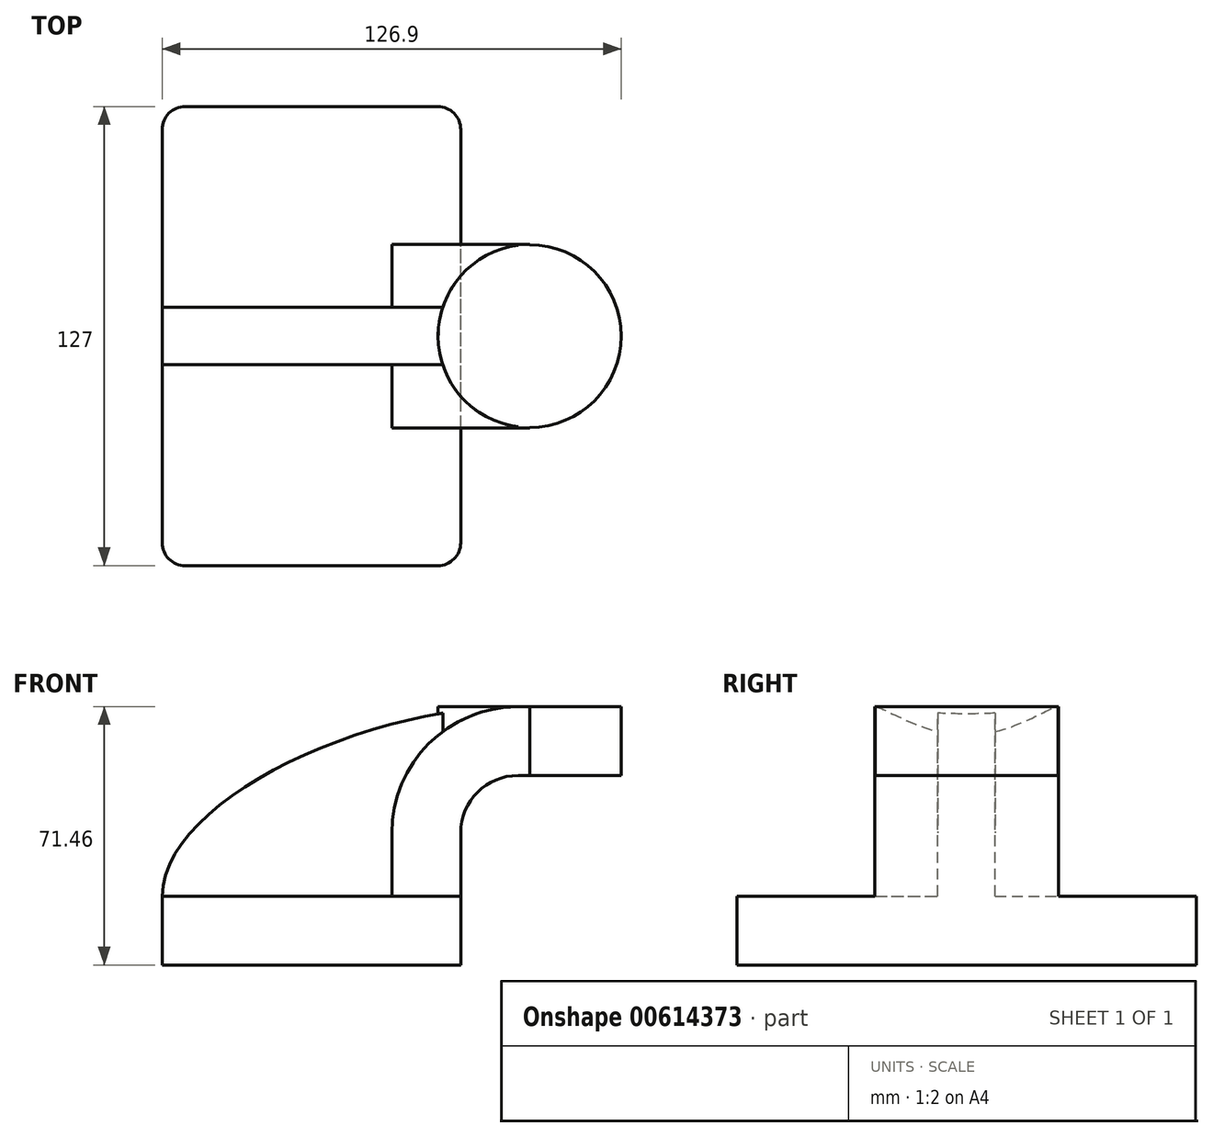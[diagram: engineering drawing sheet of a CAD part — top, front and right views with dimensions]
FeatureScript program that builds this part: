
annotation { "Feature Type Name" : "Feature", "Feature Type Description" : "" }
export const myFeature = defineFeature(function(context is Context, id is Id, definition is map)
    precondition{}
    {
        {
            var Q0;
            Q0=qCreatedBy(makeId("Front.planeOp"),FACE);
            var sketch = newSketch(context, id + "F0", { "sketchPlane" : qUnion([Q0])});
            skLineSegment(sketch, "E0.bottom", {"start": v(41.28, -9.52) * mm, "end": v(-41.28, -9.53) * mm});
            skLineSegment(sketch, "E0.top", {"start": v(41.28, 9.53) * mm, "end": v(-41.28, 9.53) * mm});
            skLineSegment(sketch, "E0.left", {"start": v(41.28, -9.52) * mm, "end": v(41.28, 9.53) * mm});
            skLineSegment(sketch, "E0.right", {"start": v(-41.28, -9.53) * mm, "end": v(-41.28, 9.53) * mm});
            skPoint(sketch, "E0.middle", {"position": v(0, 0) * mm});
            skLineSegment(sketch, "E1.bottom", {"start": v(111.12, 38.1) * mm, "end": v(60.33, 38.1) * mm});
            skLineSegment(sketch, "E1.top", {"start": v(111.12, 66.68) * mm, "end": v(60.33, 66.68) * mm});
            skLineSegment(sketch, "E1.left", {"start": v(111.12, 38.1) * mm, "end": v(111.12, 66.68) * mm});
            skLineSegment(sketch, "E1.right", {"start": v(60.33, 38.1) * mm, "end": v(60.33, 66.68) * mm});
            skPoint(sketch, "E1.middle", {"position": v(85.72, 52.39) * mm});
            skLineSegment(sketch, "E2", {"start": v(41.28, 9.53) * mm, "end": v(41.28, 27) * mm});
            skArc(sketch, "E3", {"start": v(41.27, 27) * mm, "mid": v(45.92, 38.23) * mm, "end": v(57.15, 42.88) * mm});
            skLineSegment(sketch, "E4", {"start": v(57.15, 42.88) * mm, "end": v(85.62, 42.88) * mm});
            skLineSegment(sketch, "E5.0", {"start": v(57.15, 61.93) * mm, "end": v(85.62, 61.93) * mm});
            skArc(sketch, "E5.1", {"start": v(22.22, 27) * mm, "mid": v(32.45, 51.7) * mm, "end": v(57.15, 61.93) * mm});
            skLineSegment(sketch, "E5.2", {"start": v(22.22, 9.53) * mm, "end": v(22.22, 27) * mm});
            skLineSegment(sketch, "E6", {"start": v(85.62, 42.88) * mm, "end": v(85.62, 61.93) * mm});
            skLineSegment(sketch, "E7", {"start": v(41.28, 9.53) * mm, "end": v(22.22, 9.53) * mm});
            skFitSpline(sketch, "E8", {"points": [v(-41.28, 9.52) * mm, v(57.15, 61.93) * mm], "startDerivative": vector(0.68, 80.25) * mm, "endDerivative": vector(124.58, -0.82) * mm});
            skSolve(sketch);
        }
        {
            var Q0;
            Q0=makeQuery(id+"F0.imprint","IMPRINT",FACE,{"disambiguationData":[TD([[makeQuery(id+"F0.imprint","IMPRINT",EDGE,{"derivedFrom":sQuery(id+"F0.wireOp",EDGE,"E0.bottom")}),-1.0]])]});
            extrude(context, id + "F1", {"entities" : qUnion([Q0]), "endBound" : BoundingType.SYMMETRIC, "depth" : 127 * mm, "offsetDistance" : 25.4 * mm});
        }
        {
            var Q0;
            Q0=makeQuery(id+"F0.imprint","IMPRINT",FACE,{"disambiguationData":[TD([[makeQuery(id+"F0.imprint","IMPRINT",EDGE,{"derivedFrom":sQuery(id+"F0.wireOp",EDGE,"E2")}),1.0]])]});
            extrude(context, id + "F2", {"entities" : qUnion([Q0]), "operationType" : NewBodyOperationType.ADD, "endBound" : BoundingType.SYMMETRIC, "depth" : 50.8 * mm, "offsetDistance" : 25.4 * mm});
        }
        {
            var Q0;
            Q0=makeQuery(id+"F0.imprint","IMPRINT",FACE,{"disambiguationData":[TD([[makeQuery(id+"F0.imprint","IMPRINT",EDGE,{"derivedFrom":sQuery(id+"F0.wireOp",EDGE,"E0.top")}),-1.0]])]});
            extrude(context, id + "F3", {"entities" : qUnion([Q0]), "operationType" : NewBodyOperationType.ADD, "endBound" : BoundingType.SYMMETRIC, "depth" : 15.88 * mm, "offsetDistance" : 25.4 * mm});
        }
        {
            var Q0;
            {var subQ5=sQuery(id+"F0.wireOp",EDGE,"E6");Q0=makeQuery(id+"F0.imprint","IMPRINT",FACE,{"disambiguationData":[TD([[makeQuery(id+"F0.imprint","IMPRINT",EDGE,{"derivedFrom":subQ5}),1.0]])]});}
            var Q1;
            Q1=sQuery(id+"F0.wireOp",EDGE,"E1.right");
            revolve(context, id + "F4", {"operationType" : NewBodyOperationType.ADD, "entities" : qUnion([Q0]), "axis" : qUnion([Q1]), "revolveType" : RevolveType.FULL});
        }
        {
            var Q0;
            Q0=makeQuery(id+"F1.opExtrude","CAP_EDGE",EDGE,{"disambiguationData":[OSD([sQuery(id+"F0.wireOp",EDGE,"E0.right")])],"isStart":false});
            var Q1;
            Q1=makeQuery(id+"F1.opExtrude","CAP_EDGE",EDGE,{"disambiguationData":[OSD([sQuery(id+"F0.wireOp",EDGE,"E0.left")])],"isStart":false});
            var Q2;
            Q2=makeQuery(id+"F1.opExtrude","CAP_EDGE",EDGE,{"disambiguationData":[OSD([sQuery(id+"F0.wireOp",EDGE,"E0.left")])],"isStart":true});
            var Q3;
            Q3=makeQuery(id+"F1.opExtrude","CAP_EDGE",EDGE,{"disambiguationData":[OSD([sQuery(id+"F0.wireOp",EDGE,"E0.right")])],"isStart":true});
            fillet(context, id + "F5", {"entities" : qUnion([Q0, Q1, Q2, Q3]), "radius" : 6.35 * mm, "tangentPropagation" : true, "allowEdgeOverflow" : false});
        }
    });
